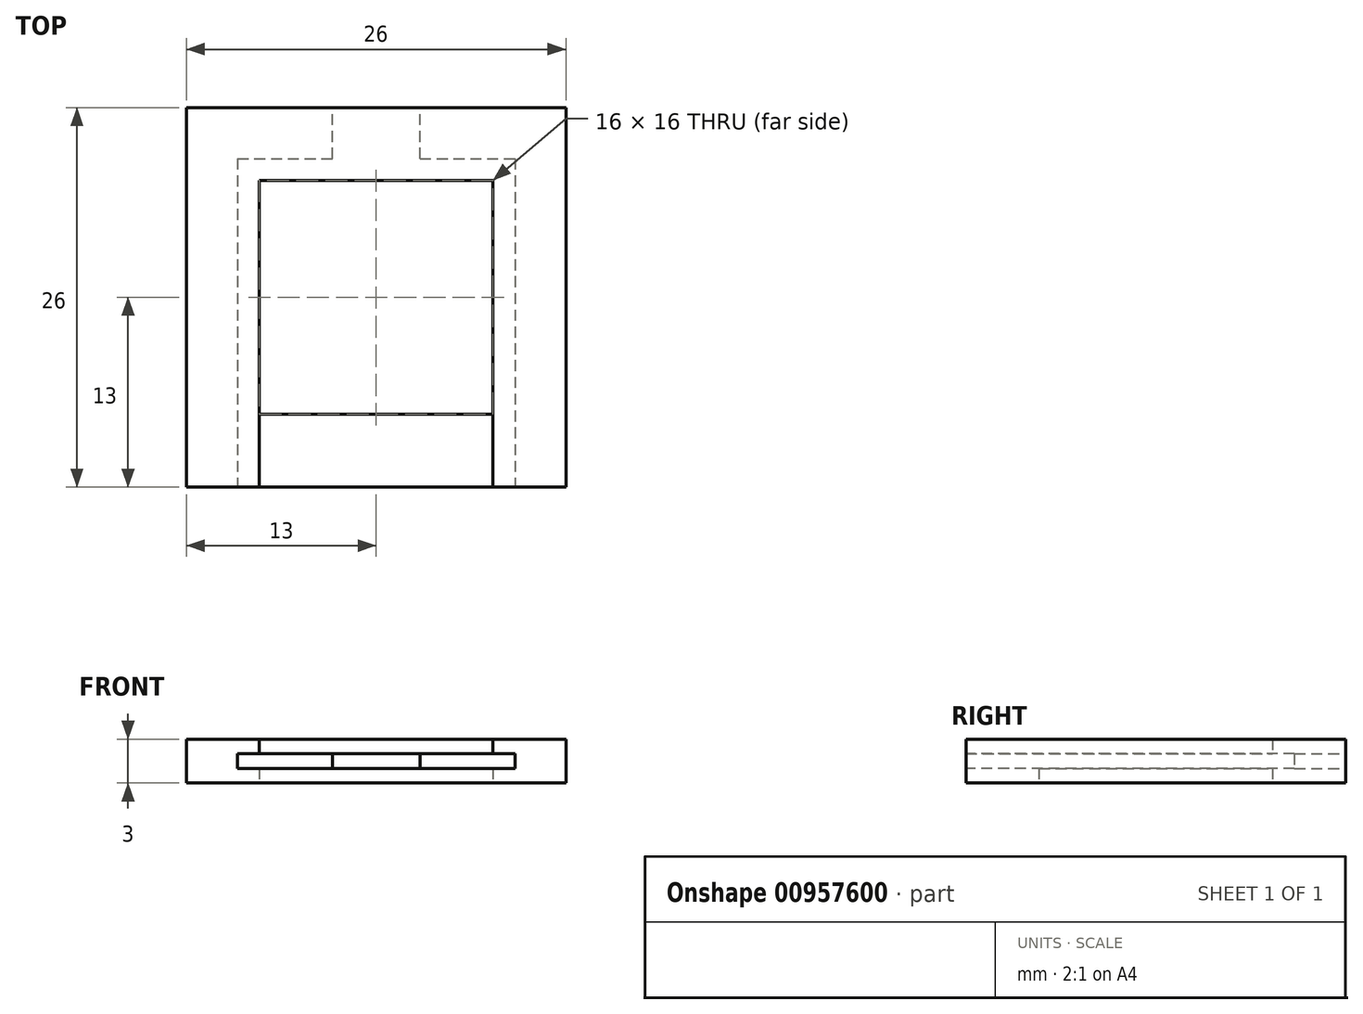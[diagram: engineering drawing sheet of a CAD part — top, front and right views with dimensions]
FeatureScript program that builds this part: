
annotation { "Feature Type Name" : "Feature", "Feature Type Description" : "" }
export const myFeature = defineFeature(function(context is Context, id is Id, definition is map)
    precondition{}
    {
        {
            var Q0;
            Q0=qCreatedBy(makeId("Top.planeOp"),FACE);
            var sketch = newSketch(context, id + "F0", { "sketchPlane" : qUnion([Q0])});
            skLineSegment(sketch, "E0.bottom", {"start": v(-13, 13) * mm, "end": v(13, 13) * mm});
            skLineSegment(sketch, "E0.top", {"start": v(-13, -13) * mm, "end": v(13, -13) * mm});
            skLineSegment(sketch, "E0.left", {"start": v(-13, 13) * mm, "end": v(-13, -13) * mm});
            skLineSegment(sketch, "E0.right", {"start": v(13, 13) * mm, "end": v(13, -13) * mm});
            skPoint(sketch, "E0.middle", {"position": v(0, 0) * mm});
            skLineSegment(sketch, "E1.bottom", {"start": v(-8, 8) * mm, "end": v(8, 8) * mm});
            skLineSegment(sketch, "E1.top", {"start": v(-8, -8) * mm, "end": v(8, -8) * mm});
            skLineSegment(sketch, "E1.left", {"start": v(-8, 8) * mm, "end": v(-8, -8) * mm});
            skLineSegment(sketch, "E1.right", {"start": v(8, 8) * mm, "end": v(8, -8) * mm});
            skSolve(sketch);
        }
        {
            var Q0;
            Q0=makeQuery(id+"F0.imprint","IMPRINT",FACE,{"disambiguationData":[TD([[makeQuery(id+"F0.imprint","IMPRINT",EDGE,{"derivedFrom":sQuery(id+"F0.wireOp",EDGE,"E0.bottom")}),-1.0]])]});
            extrude(context, id + "F1", {"entities" : qUnion([Q0]), "depth" : 3 * mm, "offsetDistance" : 25 * mm});
        }
        {
            var Q0;
            Q0=makeQuery(id+"F1.opExtrude","SWEPT_FACE",FACE,{"disambiguationData":[OSD([sQuery(id+"F0.wireOp",EDGE,"E0.top")])]});
            var sketch = newSketch(context, id + "F2", { "sketchPlane" : qUnion([Q0])});
            skLineSegment(sketch, "E2", {"start": v(-9.5, 0) * mm, "end": v(-9.5, 3) * mm, "construction": true});
            skLineSegment(sketch, "E3.MirrorCS", {"start": v(9.5, 0) * mm, "end": v(9.5, 3) * mm, "construction": true});
            skLineSegment(sketch, "E4", {"start": v(-9.5, 1.5) * mm, "end": v(9.5, 1.5) * mm, "construction": true});
            skLineSegment(sketch, "E5.bottom", {"start": v(-9.5, 2) * mm, "end": v(9.5, 2) * mm});
            skLineSegment(sketch, "E5.top", {"start": v(-9.5, 1) * mm, "end": v(9.5, 1) * mm});
            skLineSegment(sketch, "E5.left", {"start": v(-9.5, 2) * mm, "end": v(-9.5, 1) * mm});
            skLineSegment(sketch, "E5.right", {"start": v(9.5, 2) * mm, "end": v(9.5, 1) * mm});
            skPoint(sketch, "E5.middle", {"position": v(0, 1.5) * mm});
            skLineSegment(sketch, "E6", {"start": v(-8, 0) * mm, "end": v(-8, 3) * mm, "construction": true});
            skLineSegment(sketch, "E7.MirrorCS", {"start": v(8, 0) * mm, "end": v(8, 3) * mm, "construction": true});
            skLineSegment(sketch, "E8", {"start": v(-8, 3) * mm, "end": v(-8, 2) * mm});
            skLineSegment(sketch, "E9", {"start": v(-8, 2) * mm, "end": v(8, 2) * mm});
            skLineSegment(sketch, "E10", {"start": v(8, 2) * mm, "end": v(8, 3) * mm});
            skLineSegment(sketch, "E11", {"start": v(-8, 3) * mm, "end": v(8, 3) * mm});
            skSolve(sketch);
        }
        {
            var Q0;
            Q0=makeQuery(id+"F2.imprint","IMPRINT",FACE,{"disambiguationData":[TD([[makeQuery(id+"F2.imprint","IMPRINT",EDGE,{"derivedFrom":sQuery(id+"F2.wireOp",EDGE,"E5.bottom")}),-1.0]])]});
            extrude(context, id + "F3", {"entities" : qUnion([Q0]), "operationType" : NewBodyOperationType.REMOVE, "oppositeDirection" : true, "depth" : 22.5 * mm, "offsetDistance" : 25 * mm});
        }
        {
            var Q0;
            Q0=makeQuery(id+"F2.imprint","IMPRINT",FACE,{"disambiguationData":[TD([[makeQuery(id+"F2.imprint","IMPRINT",EDGE,{"derivedFrom":sQuery(id+"F2.wireOp",EDGE,"E8")}),1.0]])]});
            extrude(context, id + "F4", {"entities" : qUnion([Q0]), "operationType" : NewBodyOperationType.REMOVE, "endBound" : BoundingType.UP_TO_NEXT, "oppositeDirection" : true, "depth" : 25 * mm, "offsetDistance" : 25 * mm});
        }
        {
            var Q0;
            Q0=makeQuery(id+"F1.opExtrude","SWEPT_FACE",FACE,{"disambiguationData":[OSD([sQuery(id+"F0.wireOp",EDGE,"E0.bottom")])]});
            var sketch = newSketch(context, id + "F5", { "sketchPlane" : qUnion([Q0])});
            skLineSegment(sketch, "E12.bottom", {"start": v(-3, 2) * mm, "end": v(3, 2) * mm});
            skLineSegment(sketch, "E12.top", {"start": v(-3, 1) * mm, "end": v(3, 1) * mm});
            skLineSegment(sketch, "E12.left", {"start": v(-3, 2) * mm, "end": v(-3, 1) * mm});
            skLineSegment(sketch, "E12.right", {"start": v(3, 2) * mm, "end": v(3, 1) * mm});
            skPoint(sketch, "E12.middle", {"position": v(0, 1.5) * mm});
            skSolve(sketch);
        }
        {
            var Q0;
            Q0=makeQuery(id+"F5.imprint","IMPRINT",FACE,{"disambiguationData":[TD([[makeQuery(id+"F5.imprint","IMPRINT",EDGE,{"derivedFrom":sQuery(id+"F5.wireOp",EDGE,"E12.bottom")}),-1.0]])]});
            extrude(context, id + "F6", {"entities" : qUnion([Q0]), "operationType" : NewBodyOperationType.REMOVE, "endBound" : BoundingType.UP_TO_NEXT, "oppositeDirection" : true, "depth" : 25 * mm, "offsetDistance" : 25 * mm});
        }
    });
